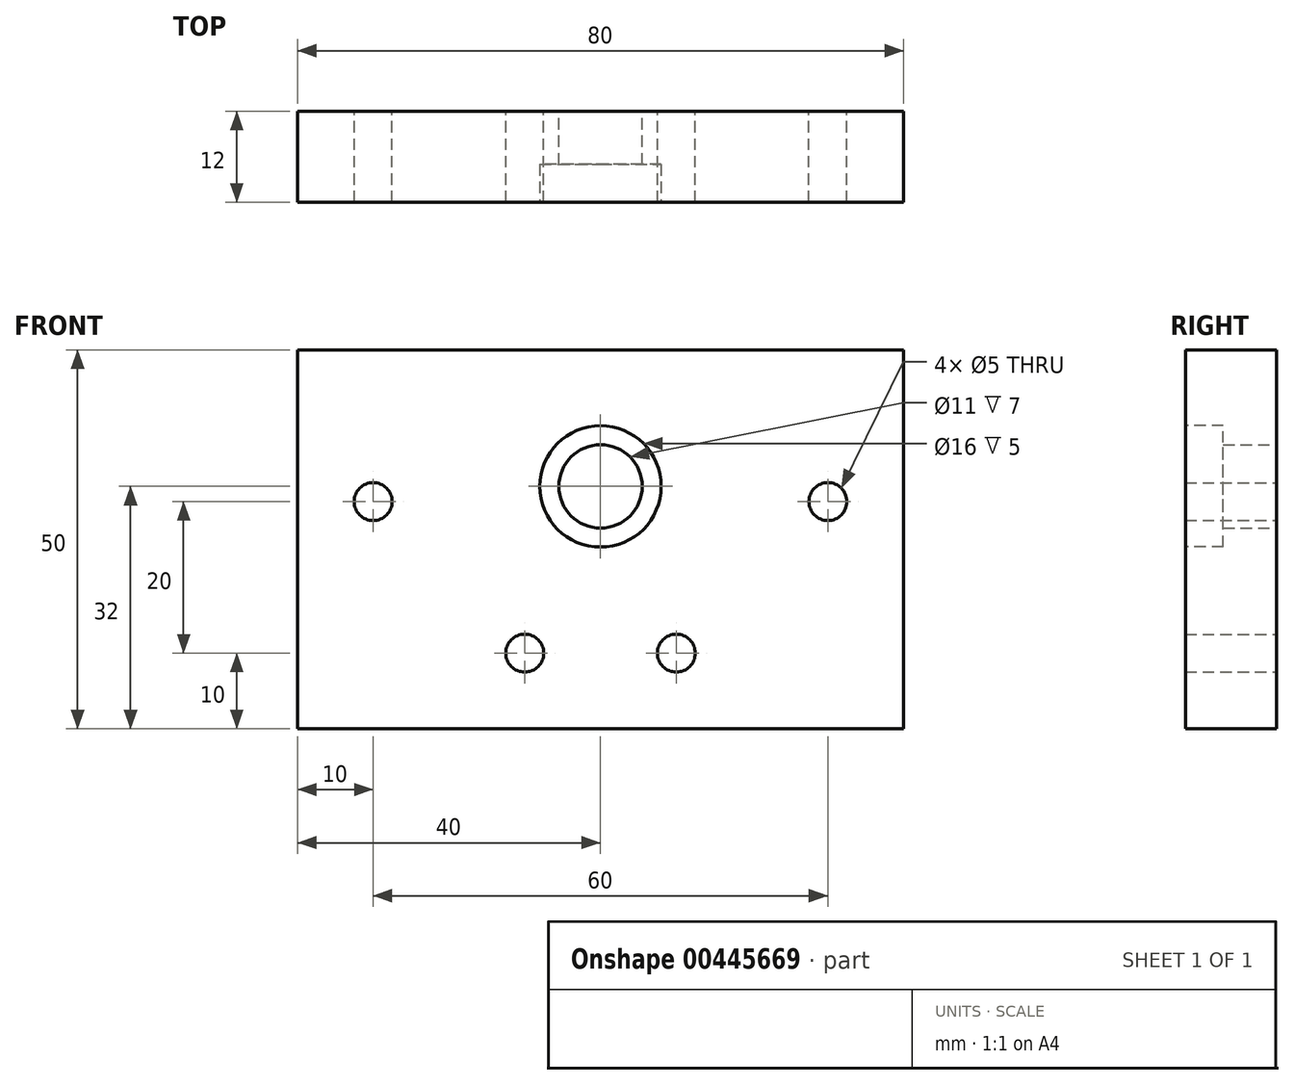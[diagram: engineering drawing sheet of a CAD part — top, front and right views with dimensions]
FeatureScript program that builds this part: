
annotation { "Feature Type Name" : "Feature", "Feature Type Description" : "" }
export const myFeature = defineFeature(function(context is Context, id is Id, definition is map)
    precondition{}
    {
        {
            var Q0;
            Q0=qCreatedBy(makeId("Front.planeOp"),FACE);
            var sketch = newSketch(context, id + "F0", { "sketchPlane" : qUnion([Q0])});
            skLineSegment(sketch, "E0.bottom", {"start": v(-40, 25) * mm, "end": v(40, 25) * mm});
            skLineSegment(sketch, "E0.top", {"start": v(-40, -25) * mm, "end": v(40, -25) * mm});
            skLineSegment(sketch, "E0.left", {"start": v(-40, 25) * mm, "end": v(-40, -25) * mm});
            skLineSegment(sketch, "E0.right", {"start": v(40, 25) * mm, "end": v(40, -25) * mm});
            skPoint(sketch, "E0.middle", {"position": v(0, 0) * mm});
            skPoint(sketch, "E1", {"position": v(-30, 5) * mm});
            skPoint(sketch, "E2.MirrorP", {"position": v(30, 5) * mm});
            skPoint(sketch, "E3", {"position": v(-10, -15) * mm});
            skPoint(sketch, "E4.MirrorP", {"position": v(10, -15) * mm});
            skCircle(sketch, "E5", {"center": v(-30, 5) * mm, "radius": 2.5 * mm});
            skCircle(sketch, "E6", {"center": v(-10, -15) * mm, "radius": 2.5 * mm});
            skCircle(sketch, "E7.MirrorC", {"center": v(30, 5) * mm, "radius": 2.5 * mm});
            skCircle(sketch, "E8.MirrorC", {"center": v(10, -15) * mm, "radius": 2.5 * mm});
            skCircle(sketch, "E9", {"center": v(0, 7) * mm, "radius": 5.5 * mm});
            skSolve(sketch);
        }
        {
            var Q0;
            Q0=qSketchRegion(id+"F0",true);
            extrude(context, id + "F1", {"entities" : qUnion([Q0]), "depth" : 12 * mm});
        }
        {
            var Q0;
            Q0=makeQuery(id+"F1.opExtrude","CAP_FACE",FACE,{"disambiguationData":[OSD([sQuery(id+"F0.wireOp",EDGE,"E0.bottom"),sQuery(id+"F0.wireOp",EDGE,"E0.top"),sQuery(id+"F0.wireOp",EDGE,"E0.left"),sQuery(id+"F0.wireOp",EDGE,"E0.right"),sQuery(id+"F0.wireOp",EDGE,"E5"),sQuery(id+"F0.wireOp",EDGE,"E6"),sQuery(id+"F0.wireOp",EDGE,"E7.MirrorC"),sQuery(id+"F0.wireOp",EDGE,"E8.MirrorC"),sQuery(id+"F0.wireOp",EDGE,"E9")])],"isStart":false});
            var sketch = newSketch(context, id + "F2", { "sketchPlane" : qUnion([Q0])});
            skCircle(sketch, "E10", {"center": v(0, 7) * mm, "radius": 8 * mm});
            skSolve(sketch);
        }
        {
            var Q0;
            Q0=makeQuery(id+"F2.imprint","IMPRINT",FACE,{"disambiguationData":[TD([[makeQuery(id+"F2.imprint","IMPRINT",EDGE,{"derivedFrom":sQuery(id+"F2.wireOp",EDGE,"E10")}),1.0]])]});
            extrude(context, id + "F3", {"entities" : qUnion([Q0]), "operationType" : NewBodyOperationType.REMOVE, "oppositeDirection" : true, "depth" : 5 * mm});
        }
    });
